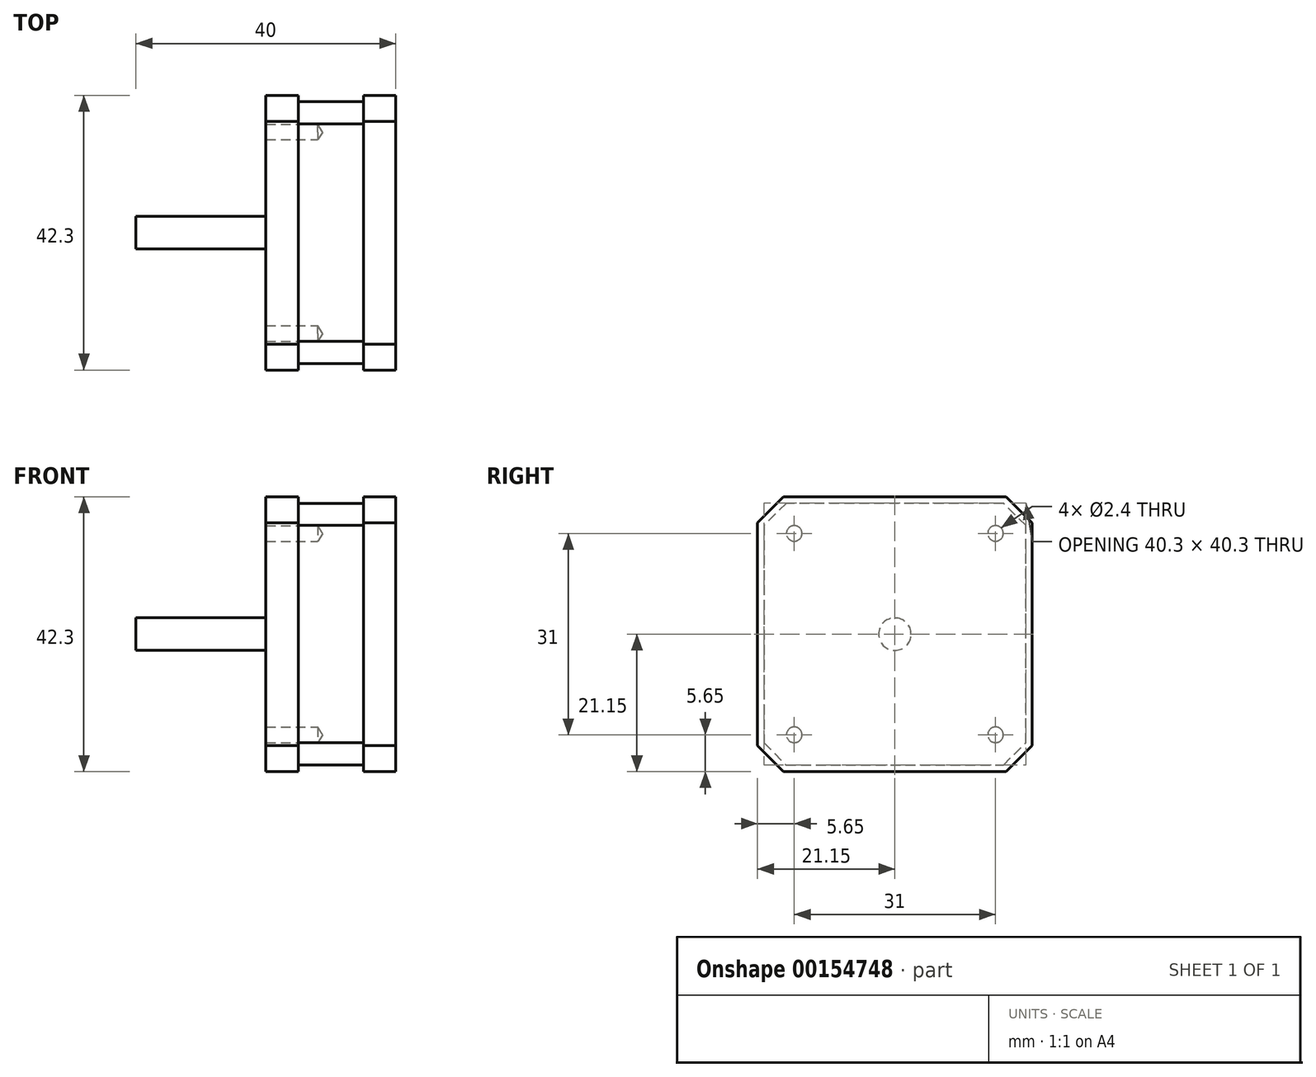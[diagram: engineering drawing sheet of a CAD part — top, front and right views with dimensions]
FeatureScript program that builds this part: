
annotation { "Feature Type Name" : "Feature", "Feature Type Description" : "" }
export const myFeature = defineFeature(function(context is Context, id is Id, definition is map)
    precondition{}
    {
        {
            var Q0;
            Q0=qCreatedBy(makeId("Right.planeOp"),FACE);
            var sketch = newSketch(context, id + "F0", { "sketchPlane" : qUnion([Q0])});
            skLineSegment(sketch, "E0.bottom", {"start": v(21.15, -21.15) * mm, "end": v(-21.15, -21.15) * mm});
            skLineSegment(sketch, "E0.top", {"start": v(21.15, 21.15) * mm, "end": v(-21.15, 21.15) * mm});
            skLineSegment(sketch, "E0.left", {"start": v(21.15, -21.15) * mm, "end": v(21.15, 21.15) * mm});
            skLineSegment(sketch, "E0.right", {"start": v(-21.15, -21.15) * mm, "end": v(-21.15, 21.15) * mm});
            skPoint(sketch, "E0.middle", {"position": v(0, 0) * mm});
            skSolve(sketch);
        }
        {
            var Q0;
            Q0 = qSketchRegion(id + "F0", true);
            extrude(context, id + "F1", {"entities" : qUnion([Q0]), "depth" : 20 * mm, "symmetric" : true});
        }
        {
            var Q0;
            Q0=makeQuery(id+"F1.opExtrude","SWEPT_EDGE",EDGE,{"disambiguationData":[OSD([sQuery(id+"F0.wireOp",EDGE,"E0.top"),sQuery(id+"F0.wireOp",EDGE,"E0.right")])]});
            var Q1;
            Q1=makeQuery(id+"F1.opExtrude","SWEPT_EDGE",EDGE,{"disambiguationData":[OSD([sQuery(id+"F0.wireOp",EDGE,"E0.top"),sQuery(id+"F0.wireOp",EDGE,"E0.left")])]});
            var Q2;
            Q2=makeQuery(id+"F1.opExtrude","SWEPT_EDGE",EDGE,{"disambiguationData":[OSD([sQuery(id+"F0.wireOp",EDGE,"E0.bottom"),sQuery(id+"F0.wireOp",EDGE,"E0.right")])]});
            var Q3;
            Q3=makeQuery(id+"F1.opExtrude","SWEPT_EDGE",EDGE,{"disambiguationData":[OSD([sQuery(id+"F0.wireOp",EDGE,"E0.bottom"),sQuery(id+"F0.wireOp",EDGE,"E0.left")])]});
            chamfer(context, id + "F2", {"entities" : qUnion([Q0, Q1, Q2, Q3]), "width" : 4 * mm, "tangentPropagation" : true});
        }
        {
            var Q0;
            Q0=qCreatedBy(makeId("Right.planeOp"),FACE);
            var sketch = newSketch(context, id + "F3", { "sketchPlane" : qUnion([Q0])});
            skLineSegment(sketch, "E1.0", {"start": v(-20.15, -16.74) * mm, "end": v(-16.74, -20.15) * mm});
            skLineSegment(sketch, "E1.1", {"start": v(-20.15, 16.74) * mm, "end": v(-20.15, -16.74) * mm});
            skLineSegment(sketch, "E1.2", {"start": v(-16.74, -20.15) * mm, "end": v(16.74, -20.15) * mm});
            skLineSegment(sketch, "E1.3", {"start": v(-16.74, 20.15) * mm, "end": v(-20.15, 16.74) * mm});
            skLineSegment(sketch, "E1.4", {"start": v(16.74, -20.15) * mm, "end": v(20.15, -16.74) * mm});
            skLineSegment(sketch, "E1.5", {"start": v(20.15, -16.74) * mm, "end": v(20.15, 16.74) * mm});
            skLineSegment(sketch, "E1.6", {"start": v(20.15, 16.74) * mm, "end": v(16.74, 20.15) * mm});
            skLineSegment(sketch, "E1.7", {"start": v(16.74, 20.15) * mm, "end": v(-16.74, 20.15) * mm});
            skLineSegment(sketch, "E2.bottom", {"start": v(21.5, -21.5) * mm, "end": v(-21.5, -21.5) * mm});
            skLineSegment(sketch, "E2.top", {"start": v(21.5, 21.5) * mm, "end": v(-21.5, 21.5) * mm});
            skLineSegment(sketch, "E2.left", {"start": v(21.5, -21.5) * mm, "end": v(21.5, 21.5) * mm});
            skLineSegment(sketch, "E2.right", {"start": v(-21.5, -21.5) * mm, "end": v(-21.5, 21.5) * mm});
            skPoint(sketch, "E2.middle", {"position": v(0, 0) * mm});
            skSolve(sketch);
        }
        {
            var Q0;
            Q0 = qSketchRegion(id + "F3", true);
            extrude(context, id + "F4", {"entities" : qUnion([Q0]), "operationType" : NewBodyOperationType.REMOVE, "oppositeDirection" : true, "depth" : 10 * mm, "symmetric" : true});
        }
        {
            var Q0;
            Q0=makeQuery(id+"F1.opExtrude","CAP_FACE",FACE,{"disambiguationData":[OSD([sQuery(id+"F0.wireOp",EDGE,"E0.bottom"),sQuery(id+"F0.wireOp",EDGE,"E0.top"),sQuery(id+"F0.wireOp",EDGE,"E0.left"),sQuery(id+"F0.wireOp",EDGE,"E0.right")])],"isStart":true});
            var sketch = newSketch(context, id + "F5", { "sketchPlane" : qUnion([Q0])});
            skCircle(sketch, "E3", {"center": v(0, 0) * mm, "radius": 2.5 * mm});
            skSolve(sketch);
        }
        {
            var Q0;
            Q0 = qSketchRegion(id + "F5", true);
            extrude(context, id + "F6", {"entities" : qUnion([Q0]), "operationType" : NewBodyOperationType.ADD, "depth" : 20 * mm});
        }
        {
            var Q0;
            Q0=makeQuery(id+"F1.opExtrude","CAP_FACE",FACE,{"disambiguationData":[OSD([sQuery(id+"F0.wireOp",EDGE,"E0.bottom"),sQuery(id+"F0.wireOp",EDGE,"E0.top"),sQuery(id+"F0.wireOp",EDGE,"E0.left"),sQuery(id+"F0.wireOp",EDGE,"E0.right")])],"isStart":true});
            var sketch = newSketch(context, id + "F7", { "sketchPlane" : qUnion([Q0])});
            skPoint(sketch, "E4", {"position": v(-15.5, 15.5) * mm});
            skPoint(sketch, "E5.0.1.0", {"position": v(-15.5, -15.5) * mm});
            skPoint(sketch, "E5.1.0.0", {"position": v(15.5, 15.5) * mm});
            skPoint(sketch, "E5.1.1.0", {"position": v(15.5, -15.5) * mm});
            skLineSegment(sketch, "E5.direction1", {"start": v(-15.5, 15.5) * mm, "end": v(15.5, 15.5) * mm, "construction": true});
            skLineSegment(sketch, "E5.direction2", {"start": v(-15.5, 15.5) * mm, "end": v(-15.5, -15.5) * mm, "construction": true});
            skSolve(sketch);
        }
        {
            var Q0;
            Q0=sQuery(id+"F7.wireOp",VERTEX,"E4");
            var Q1;
            Q1=sQuery(id+"F7.wireOp",VERTEX,"E5.1.0.0");
            var Q2;
            Q2=sQuery(id+"F7.wireOp",VERTEX,"E5.0.1.0");
            var Q3;
            Q3=sQuery(id+"F7.wireOp",VERTEX,"E5.1.1.0");
            var Q4;
            Q4=makeQuery(id+"F1.opExtrude","SWEPT_BODY",BODY,{"disambiguationData":[OSD([sQuery(id+"F0.wireOp",EDGE,"E0.bottom"),sQuery(id+"F0.wireOp",EDGE,"E0.top"),sQuery(id+"F0.wireOp",EDGE,"E0.left"),sQuery(id+"F0.wireOp",EDGE,"E0.right")])]});
            hole(context, id + "F8", {"style" : HoleStyle.SIMPLE, "endStyle" : HoleEndStyle.BLIND, "standardTappedOrClearance" : lookupTablePath({ "standard" : "ISO", "engagement" : "75%", "pitch" : "0.6 mm", "size" : "M3", "type" : "Tapped" }), "standardBlindInLast" : lookupTablePath({ "standard" : "ISO", "engagement" : "75%", "pitch" : "0.6 mm", "size" : "M3", "type" : "Tapped" }), "holeDiameter" : 2.4 * mm, "holeDepth" : 8 * mm, "locations" : qUnion([Q0, Q1, Q2, Q3]), "scope" : qUnion([Q4]), "startStyle" : HoleStartStyle.PART});
        }
    });
